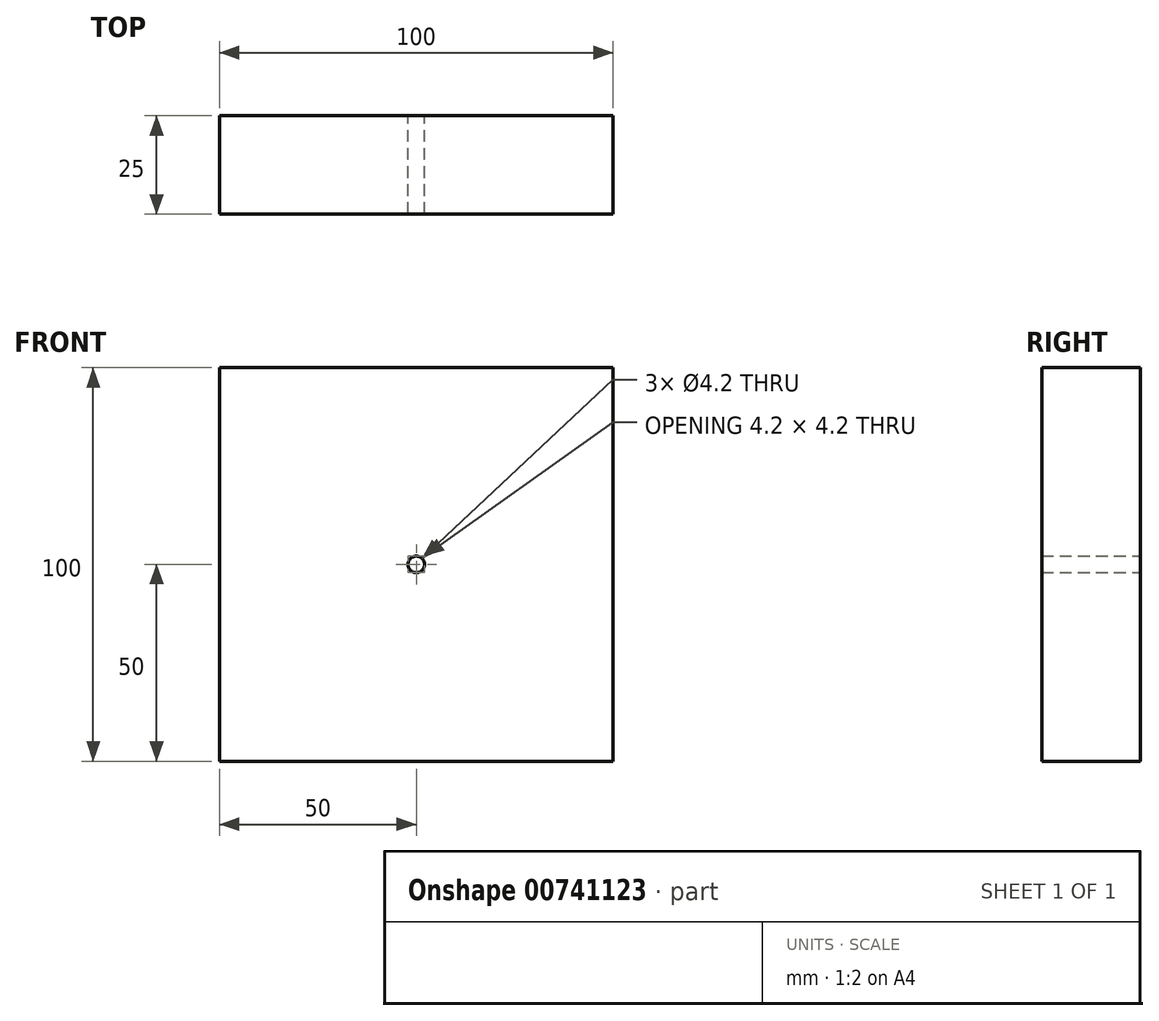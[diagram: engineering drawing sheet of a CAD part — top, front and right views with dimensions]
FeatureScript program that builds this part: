
annotation { "Feature Type Name" : "Feature", "Feature Type Description" : "" }
export const myFeature = defineFeature(function(context is Context, id is Id, definition is map)
    precondition{}
    {
        {
            var Q0;
            Q0=qCreatedBy(makeId("Front.planeOp"),FACE);
            var sketch = newSketch(context, id + "F0", { "sketchPlane" : qUnion([Q0])});
            skLineSegment(sketch, "E0.bottom", {"start": v(50, -50) * mm, "end": v(-50, -50) * mm});
            skLineSegment(sketch, "E0.top", {"start": v(50, 50) * mm, "end": v(-50, 50) * mm});
            skLineSegment(sketch, "E0.left", {"start": v(50, -50) * mm, "end": v(50, 50) * mm});
            skLineSegment(sketch, "E0.right", {"start": v(-50, -50) * mm, "end": v(-50, 50) * mm});
            skPoint(sketch, "E0.middle", {"position": v(0, 0) * mm});
            skSolve(sketch);
        }
        {
            var Q0;
            Q0=makeQuery(id+"F0.imprint","IMPRINT",FACE,{"disambiguationData":[TD([[makeQuery(id+"F0.imprint","IMPRINT",EDGE,{"derivedFrom":sQuery(id+"F0.wireOp",EDGE,"E0.bottom")}),-1.0]])]});
            extrude(context, id + "F1", {"entities" : qUnion([Q0]), "depth" : 25 * mm, "offsetDistance" : 25 * mm});
        }
        {
            var Q0;
            Q0=sQuery(id+"F0.wireOp",VERTEX,"E0.middle");
            var Q1;
            Q1=makeQuery(id+"F1.opExtrude","SWEPT_BODY",BODY,{"disambiguationData":[OSD([sQuery(id+"F0.wireOp",EDGE,"E0.bottom"),sQuery(id+"F0.wireOp",EDGE,"E0.top"),sQuery(id+"F0.wireOp",EDGE,"E0.left"),sQuery(id+"F0.wireOp",EDGE,"E0.right")])]});
            hole(context, id + "F2", {"style" : HoleStyle.SIMPLE, "endStyle" : HoleEndStyle.THROUGH, "oppositeDirection" : true, "standardTappedOrClearance" : lookupTablePath({ "standard" : "ISO", "engagement" : "75%", "pitch" : "0.8 mm", "size" : "M5", "type" : "Tapped" }), "standardBlindInLast" : lookupTablePath({ "standard" : "ISO", "engagement" : "75%", "pitch" : "0.8 mm", "size" : "M5", "type" : "Tapped" }), "holeDiameter" : 4.2 * mm, "majorDiameter" : 5 * mm, "showTappedDepth" : true, "isTappedThrough" : true, "tappedDepth" : 23.1 * mm, "tapClearance" : 3, "locations" : qUnion([Q0]), "scope" : qUnion([Q1])});
        }
    });
